# Revit family: Schienenklammer
name_source: partatom
category: HLS-Bauteile
revit_build: Autodesk Revit 2017 (Build: 20190507_1515(x64)
units: mm (PartAtom-declared; Revit-internal decimal feet)

## family parameters
Arbeitsebenenbasiert = Ja
Beim Laden mit Abzugskörper schneiden = Nein
Bemaßung runder Anschluss = Durchmesser verwenden
Gemeinsam genutzt = Ja
Immer vertikal = Nein
Raumberechnungspunkt = Nein
Teiletyp = Normal

## types (1)
- Schienenklammer
    Artikelnummer = 0816477
    Breite = 30 mm  [stored 0.0984252 ft]
    EAN = 4250928420336
    Fabrikat = MEFA
    Firma = MEFA Befestigungs- und Montagesysteme GmbH
    Gewicht = 0.23 kg
    Gewicht pro Bauteil = 0.23 kg
    Höhe = 26 mm
    Kurztext1 = Schienenklammer C-Profil 35-45
    Kurztext2 = max. Klemmdicke 23 mm
    Material = Stahl
    Materialname = St 44-2
    Mengeneinheit = St
    Oberflaeche = galvanisch verzinkt
    Setztiefe = M12, SW 19
    Stärke = 6 mm  [stored 0.019685 ft]
    Typ Mutter = M12x50, SW19
    Vorgabe-Ansicht = 1219 mm
    Vorspannung = 8 Nm
    max Klemmdicke = 23 mm  [stored 0.0754593 ft]
    max. zul. Last = 5.00 kN
    min. Klemmdicke = 23 mm
    vpe = 20 St

note: [stored X ft] marks values corroborated as IEEE doubles in the binary element streams (Revit-internal decimal feet)

## geometry (parser evidence)
native form markers: Sweep x3
no freeform markers — native parametric forms only
